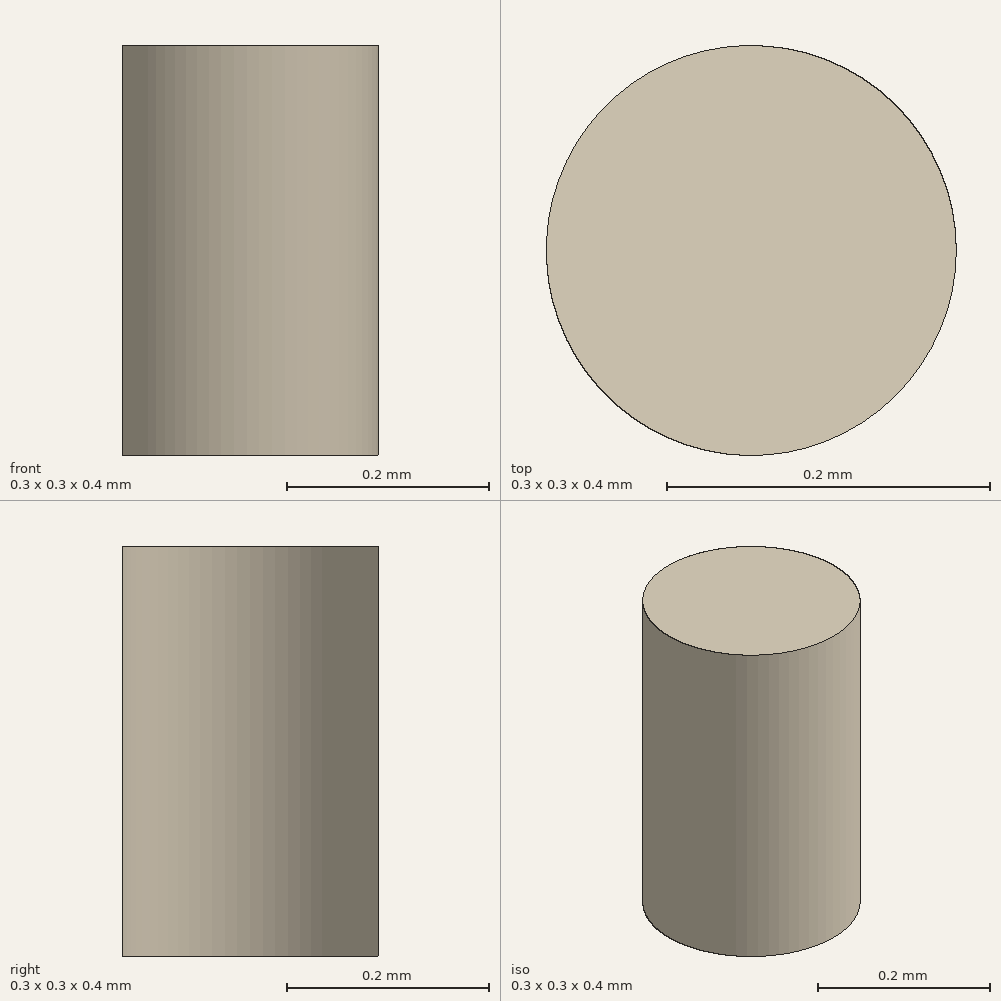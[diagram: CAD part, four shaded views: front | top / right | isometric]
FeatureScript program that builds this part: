
annotation { "Feature Type Name" : "Feature", "Feature Type Description" : "" }
export const myFeature = defineFeature(function(context is Context, id is Id, definition is map)
    precondition{}
    {
        {
            var Q0;
            Q0=qCreatedBy(makeId("Top.planeOp"),FACE);
            var sketch = newSketch(context, id + "F0", { "sketchPlane" : qUnion([Q0])});
            skCircle(sketch, "E0", {"center": v(0, 0) * mm, "radius": 0.13 * mm});
            skSolve(sketch);
        }
        {
            var Q0;
            Q0=makeQuery(id+"F0.imprint","IMPRINT",FACE,{"disambiguationData":[TD([[makeQuery(id+"F0.imprint","IMPRINT",EDGE,{"derivedFrom":sQuery(id+"F0.wireOp",EDGE,"E0")}),1.0]])]});
            extrude(context, id + "F1", {"entities" : qUnion([Q0]), "depth" : 0.4 * mm});
        }
    });
